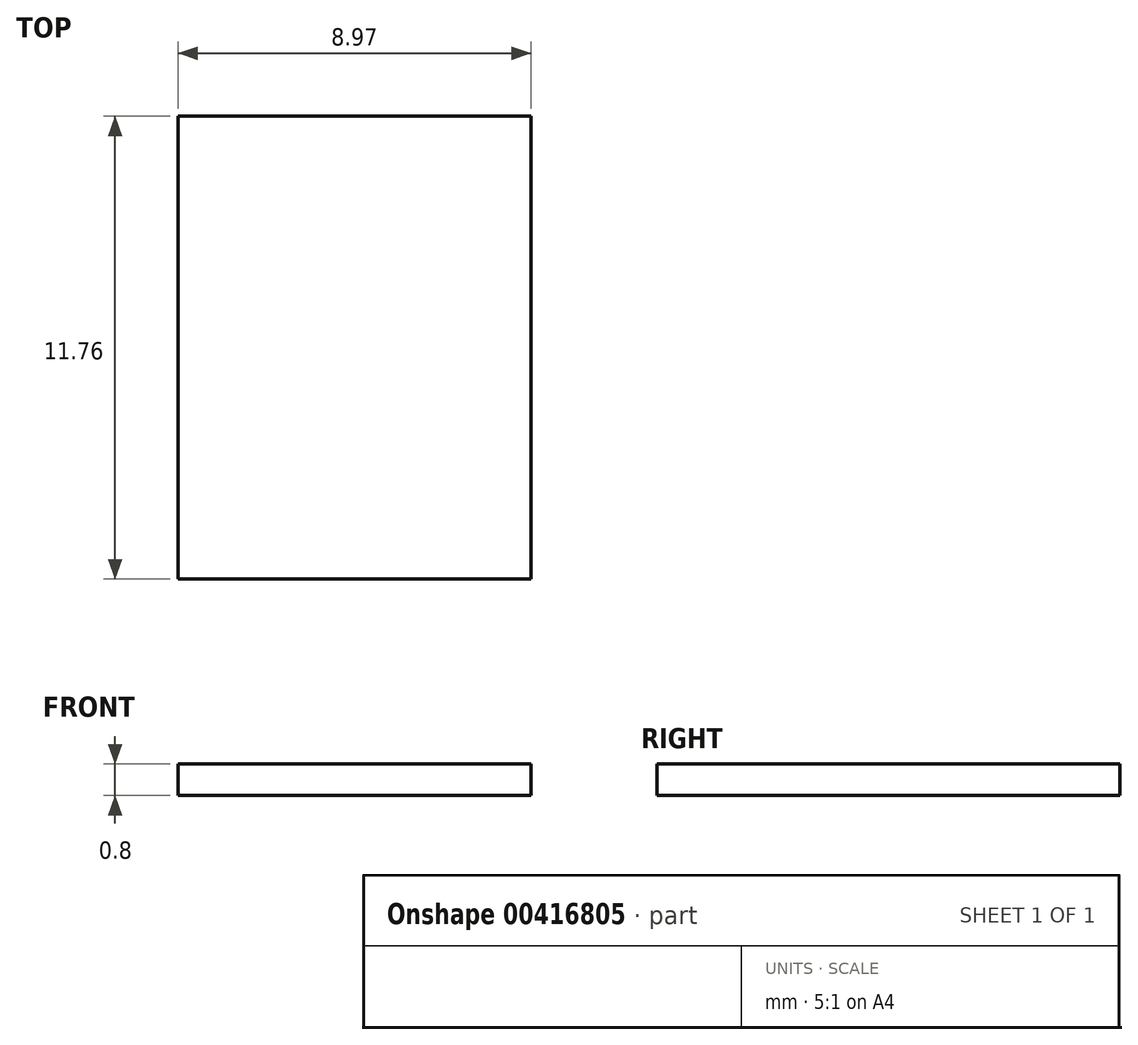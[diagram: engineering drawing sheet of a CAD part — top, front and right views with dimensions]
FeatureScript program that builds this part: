
annotation { "Feature Type Name" : "Feature", "Feature Type Description" : "" }
export const myFeature = defineFeature(function(context is Context, id is Id, definition is map)
    precondition{}
    {
        {
            var Q0;
            Q0=qCreatedBy(makeId("Top.planeOp"),FACE);
            var sketch = newSketch(context, id + "F0", { "sketchPlane" : qUnion([Q0])});
            skLineSegment(sketch, "E0.bottom", {"start": v(0, 0) * mm, "end": v(8.97, 0) * mm});
            skLineSegment(sketch, "E0.top", {"start": v(0, 11.76) * mm, "end": v(8.97, 11.76) * mm});
            skLineSegment(sketch, "E0.left", {"start": v(0, 0) * mm, "end": v(0, 11.76) * mm});
            skLineSegment(sketch, "E0.right", {"start": v(8.97, 0) * mm, "end": v(8.97, 11.76) * mm});
            skSolve(sketch);
        }
        {
            var Q0;
            Q0=makeQuery(id+"F0.imprint","IMPRINT",FACE,{"disambiguationData":[TD([[makeQuery(id+"F0.imprint","IMPRINT",EDGE,{"derivedFrom":sQuery(id+"F0.wireOp",EDGE,"E0.bottom")}),1.0]])]});
            extrude(context, id + "F1", {"entities" : qUnion([Q0]), "depth" : .8 * mm, "offsetDistance" : 25.4 * mm});
        }
    });
